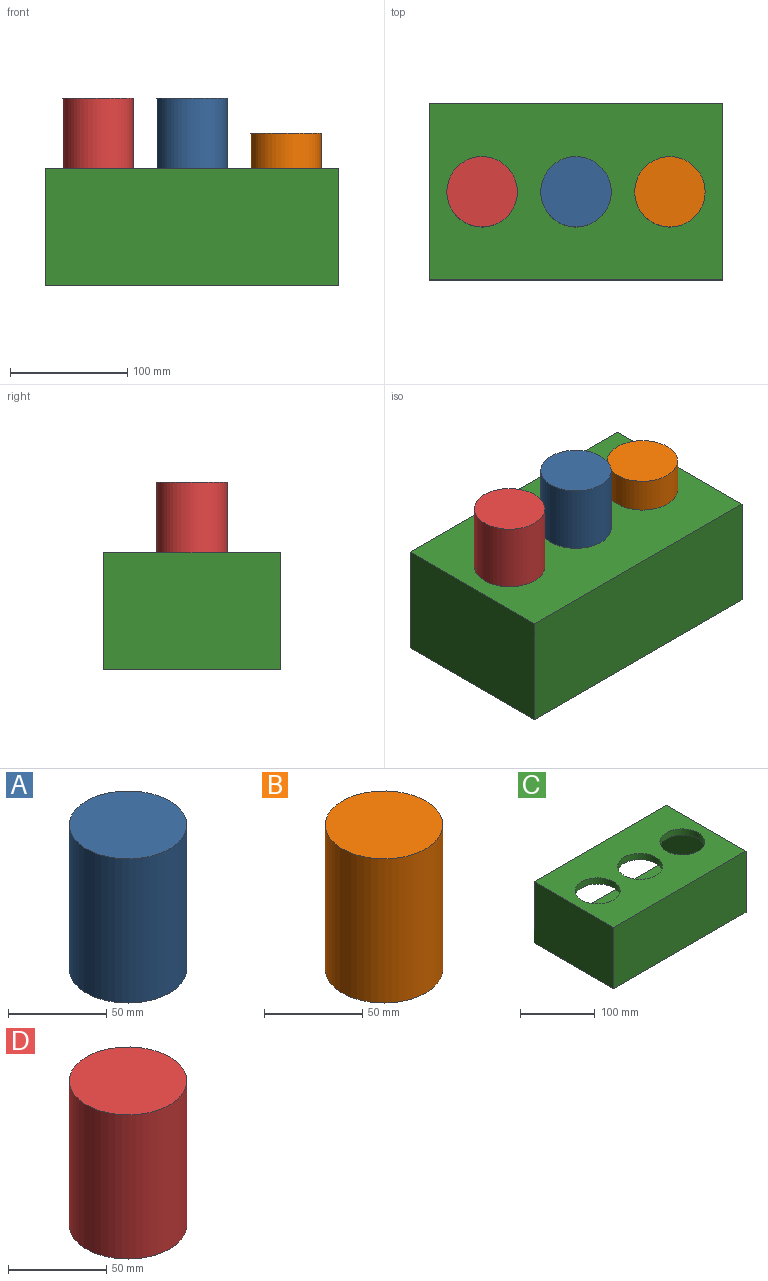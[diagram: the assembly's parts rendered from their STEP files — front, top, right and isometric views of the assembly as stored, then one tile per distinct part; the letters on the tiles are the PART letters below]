
ASSEMBLY  parts=4 mates=3
PART A: 3 faces, bbox 60x60x90 mm
  f0: cylinder r=30mm len=90mm, axis (0,0,1), area 16964.6mm2, adj f1,f2
  f1: plane 60x60mm, normal (0,0,-1), area 2827.4mm2, adj f0
  f2: plane 60x60mm, normal (0,0,1), area 2827.4mm2, adj f0
PART B: 3 faces, bbox 60x60x90 mm
  f0: cylinder r=30mm len=90mm, axis (0,0,1), area 16964.6mm2, adj f1,f2
  f1: plane 60x60mm, normal (0,0,-1), area 2827.4mm2, adj f0
  f2: plane 60x60mm, normal (0,0,1), area 2827.4mm2, adj f0
PART C: 14 faces, bbox 250x150x100 mm
  f0: plane 250x100mm, normal (0,1,0), area 6600mm2, adj f1,f3,f4,f5,f6,f8,f9,f10
  f1: plane 150x100mm, normal (-1,0,0), area 15000mm2, adj f0,f2,f4,f5
  f2: plane 250x100mm, normal (0,-1,0), area 25000mm2, adj f1,f3,f4,f5
  f3: plane 150x100mm, normal (1,0,0), area 15000mm2, adj f0,f2,f4,f5
  f4: plane 250x150mm, normal (0,0,1), area 29017.7mm2, adj f0,f1,f2,f3,f11,f12,f13
  f5: plane 250x150mm, normal (0,0,-1), area 37500mm2, adj f0,f1,f2,f3
  f6: plane 140x80mm, normal (1,0,0), area 11200mm2, adj f0,f7,f9,f10
  f7: plane 230x80mm, normal (0,1,0), area 18400mm2, adj f6,f8,f9,f10
  f8: plane 140x80mm, normal (-1,0,0), area 11200mm2, adj f0,f7,f9,f10
  f9: plane 230x140mm, normal (0,0,-1), area 23717.7mm2, adj f0,f6,f7,f8,f11,f12,f13
  f10: plane 230x140mm, normal (0,0,1), area 32200mm2, adj f0,f6,f7,f8
  f11: cylinder r=30mm len=60mm, axis (0,0,1), area 1885mm2, adj f4,f9
  f12: cylinder r=30mm len=60mm, axis (0,0,1), area 1885mm2, adj f4,f9
  f13: cylinder r=30mm len=60mm, axis (0,0,1), area 1885mm2, adj f4,f9
PART D: 3 faces, bbox 60x60x90 mm
  f0: cylinder r=30mm len=90mm, axis (0,0,1), area 16964.6mm2, adj f1,f2
  f1: plane 60x60mm, normal (0,0,-1), area 2827.4mm2, adj f0
  f2: plane 60x60mm, normal (0,0,1), area 2827.4mm2, adj f0
PLACE A t=(80,0,15)mm
PLACE B t=(0,0,-15)mm
PLACE C at identity fixed
PLACE D t=(-80,0,15)mm
MATE slider C.f13 <-> B.f0  axis (0,0,1) through (80,0,100)mm
MATE slider C.f12 <-> D.f0  axis (0,0,1) through (-80,0,100)mm
MATE slider C.f11 <-> A.f0  axis (0,0,1) through (0,0,100)mm
